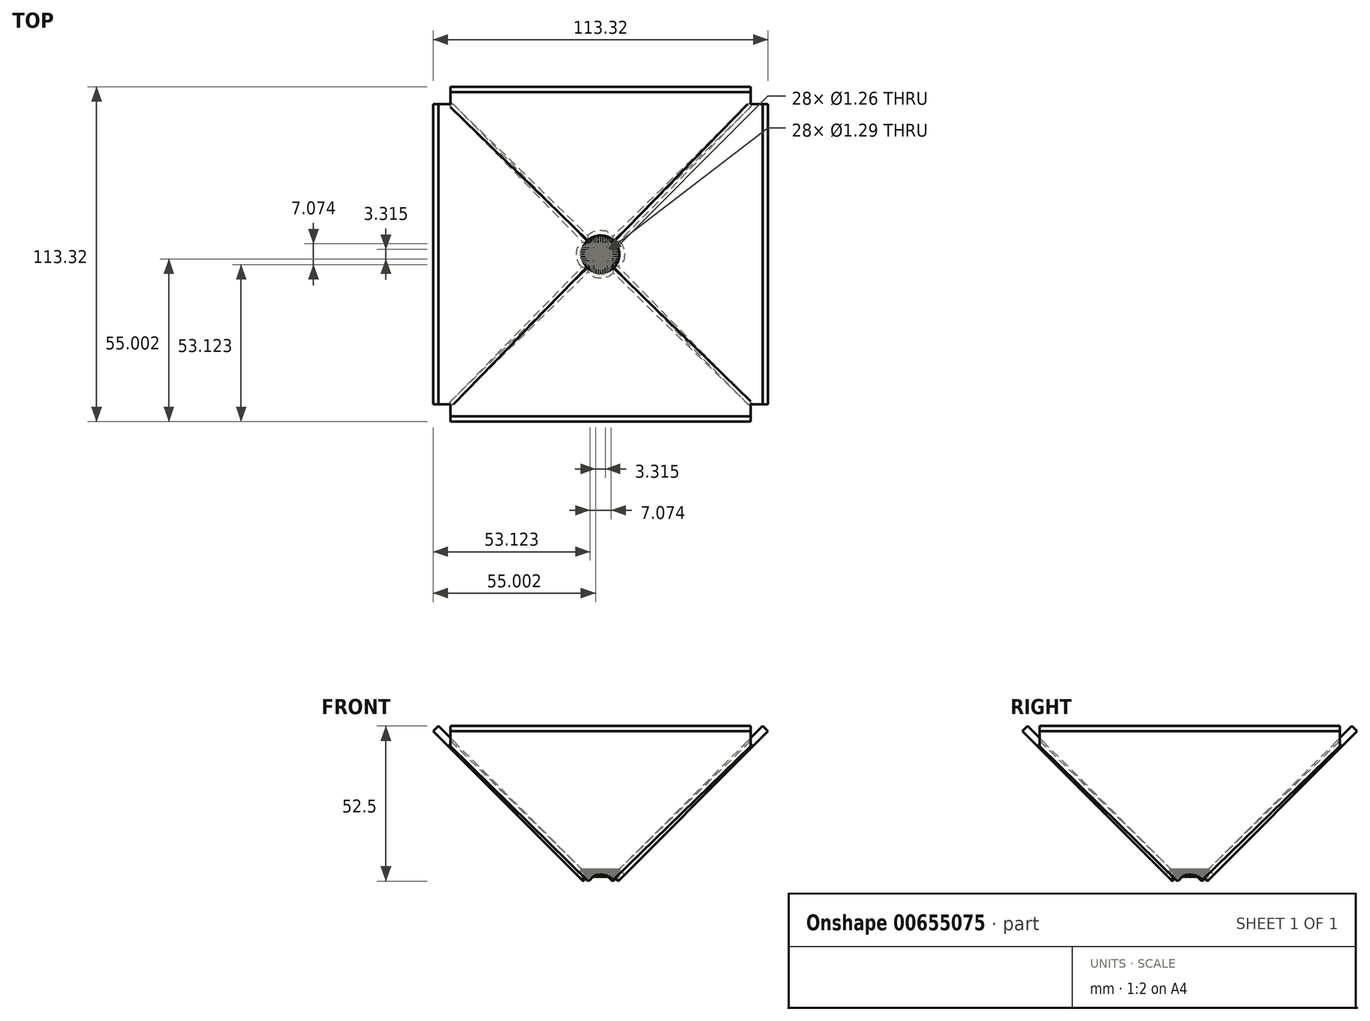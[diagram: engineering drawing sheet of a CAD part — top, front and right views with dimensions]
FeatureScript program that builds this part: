
annotation { "Feature Type Name" : "Feature", "Feature Type Description" : "" }
export const myFeature = defineFeature(function(context is Context, id is Id, definition is map)
    precondition{}
    {
        {
            var Q0;
            Q0=qCreatedBy(makeId("Top.planeOp"),FACE);
            cPlane(context, id + "F0", {"entities" : qUnion([Q0]), "cplaneType" : CPlaneType.OFFSET, "offset" : 38.1 * mm, "oppositeDirection" : true, "width" : 152.4 * mm, "height" : 152.4 * mm});
        }
        {
            var Q0;
            Q0=qCreatedBy(id+"F0.planeOp",FACE);
            var sketch = newSketch(context, id + "F1", { "sketchPlane" : qUnion([Q0])});
            skCircle(sketch, "E0", {"center": v(0, 0) * mm, "radius": 6.35 * mm});
            skCircle(sketch, "E1", {"center": v(-3.67, 3.36) * mm, "radius": 0.6 * mm});
            skCircle(sketch, "E2", {"center": v(-2.54, 2.49) * mm, "radius": 0.63 * mm});
            skCircle(sketch, "E3", {"center": v(-1.1, 1.24) * mm, "radius": 0.65 * mm});
            skCircle(sketch, "E4.1.0", {"center": v(-1.66, -0.08) * mm, "radius": 0.65 * mm});
            skCircle(sketch, "E4.1.1", {"center": v(-3.53, -0.43) * mm, "radius": 0.63 * mm});
            skCircle(sketch, "E4.1.2", {"center": v(-4.92, -0.77) * mm, "radius": 0.6 * mm});
            skCircle(sketch, "E4.2.0", {"center": v(-0.97, -1.35) * mm, "radius": 0.65 * mm});
            skCircle(sketch, "E4.2.1", {"center": v(-1.86, -3.03) * mm, "radius": 0.63 * mm});
            skCircle(sketch, "E4.2.2", {"center": v(-2.46, -4.33) * mm, "radius": 0.6 * mm});
            skCircle(sketch, "E4.3.0", {"center": v(0.45, -1.6) * mm, "radius": 0.65 * mm});
            skCircle(sketch, "E4.3.1", {"center": v(1.2, -3.34) * mm, "radius": 0.63 * mm});
            skCircle(sketch, "E4.3.2", {"center": v(1.85, -4.62) * mm, "radius": 0.6 * mm});
            skCircle(sketch, "E4.4.0", {"center": v(1.53, -0.65) * mm, "radius": 0.65 * mm});
            skCircle(sketch, "E4.4.1", {"center": v(3.37, -1.14) * mm, "radius": 0.63 * mm});
            skCircle(sketch, "E4.4.2", {"center": v(4.77, -1.44) * mm, "radius": 0.6 * mm});
            skCircle(sketch, "E4.5.0", {"center": v(1.46, 0.8) * mm, "radius": 0.65 * mm});
            skCircle(sketch, "E4.5.1", {"center": v(3, 1.92) * mm, "radius": 0.63 * mm});
            skCircle(sketch, "E4.5.2", {"center": v(4.1, 2.83) * mm, "radius": 0.6 * mm});
            skCircle(sketch, "E4.6.0", {"center": v(0.29, 1.63) * mm, "radius": 0.65 * mm});
            skCircle(sketch, "E4.6.1", {"center": v(0.36, 3.54) * mm, "radius": 0.63 * mm});
            skCircle(sketch, "E4.6.2", {"center": v(0.34, 4.97) * mm, "radius": 0.6 * mm});
            skSolve(sketch);
        }
        {
            var Q0;
            Q0=makeQuery(id+"F1.imprint","IMPRINT",FACE,{"disambiguationData":[TD([[makeQuery(id+"F1.imprint","IMPRINT",EDGE,{"derivedFrom":sQuery(id+"F1.wireOp",EDGE,"E0")}),1.0]])]});
            extrude(context, id + "F2", {"entities" : qUnion([Q0]), "oppositeDirection" : true, "depth" : 2.54 * mm, "offsetDistance" : 25.4 * mm});
        }
        {
            var Q0;
            Q0=qCreatedBy(id+"F0.planeOp",FACE);
            var sketch = newSketch(context, id + "F3", { "sketchPlane" : qUnion([Q0])});
            skLineSegment(sketch, "E5", {"start": v(6.33, -19.76) * mm, "end": v(6.33, 23.67) * mm});
            skSolve(sketch);
        }
        {
            var Q0;
            Q0=sQuery(id+"F3.wireOp",EDGE,"E5");
            cPlane(context, id + "F4", {"entities" : qUnion([Q0]), "cplaneType" : CPlaneType.LINE_ANGLE, "offset" : 25.4 * mm, "angle" : 135 * degree, "width" : 152.4 * mm, "height" : 152.4 * mm});
        }
        {
            var Q0;
            Q0=qCreatedBy(id+"F4.planeOp",FACE);
            var sketch = newSketch(context, id + "F5", { "sketchPlane" : qUnion([Q0])});
            skPoint(sketch, "E6.middle", {"position": v(0, 78.38) * mm});
            skLineSegment(sketch, "E7", {"start": v(50.8, 46.18) * mm, "end": v(50.8, 27.28) * mm});
            skLineSegment(sketch, "E8", {"start": v(-50.8, 46.18) * mm, "end": v(-50.8, 27.28) * mm});
            skPoint(sketch, "E9.start.orphan", {"position": v(0, -23.24) * mm});
            skLineSegment(sketch, "E10", {"start": v(-2.65, -23.26) * mm, "end": v(-2.65, -23.26) * mm});
            skLineSegment(sketch, "E11", {"start": v(50.8, 27.28) * mm, "end": v(5.34, -26.59) * mm});
            skFitSpline(sketch, "E12", {"points": [v(5.34, -26.59) * mm, v(4.35, -24.93) * mm, v(2.54, -23.2) * mm, v(0.28, -22.42) * mm, v(-0.8, -22.57) * mm, v(-2.12, -22.95) * mm, v(-4.13, -25.53) * mm, v(-5.03, -25.92) * mm], "startDerivative": vector(-6.1, 11.5) * mm, "endDerivative": vector(-5.47, -9.85) * mm});
            skLineSegment(sketch, "E13", {"start": v(-5.03, -25.92) * mm, "end": v(-50.8, 27.28) * mm});
            skPoint(sketch, "E6.bottom.start.orphan", {"position": v(50.8, 91.67) * mm});
            skPoint(sketch, "E6.right.start.orphan", {"position": v(-50.8, 91.67) * mm});
            skLineSegment(sketch, "E14", {"start": v(50.8, 46.18) * mm, "end": v(-50.8, 46.18) * mm});
            skPoint(sketch, "E15.orphan", {"position": v(50.8, 65.08) * mm});
            skPoint(sketch, "E16.orphan", {"position": v(-50.8, 65.08) * mm});
            skLineSegment(sketch, "E17", {"start": v(50.8, 39.03) * mm, "end": v(4.35, -24.93) * mm});
            skLineSegment(sketch, "E18", {"start": v(-50.8, 39.04) * mm, "end": v(-4.13, -25.53) * mm});
            skSolve(sketch);
        }
        {
            var Q0;
            {var subQ0=sQuery(id+"F5.wireOp",EDGE,"E14");Q0=makeQuery(id+"F5.imprint","IMPRINT",FACE,{"disambiguationData":[TD([[makeQuery(id+"F5.imprint","IMPRINT",EDGE,{"derivedFrom":subQ0}),1.0]])]});}
            extrude(context, id + "F6", {"entities" : qUnion([Q0]), "operationType" : NewBodyOperationType.ADD, "depth" : 2.54 * mm, "offsetDistance" : 25.4 * mm});
        }
        {
            var Q0;
            Q0=qCreatedBy(makeId("Front.planeOp"),FACE);
            var sketch = newSketch(context, id + "F7", { "sketchPlane" : qUnion([Q0])});
            skLineSegment(sketch, "E19", {"start": v(0, 0) * mm, "end": v(0, -3.64) * mm});
            skLineSegment(sketch, "E20", {"start": v(0, -34.92) * mm, "end": v(0, 0) * mm});
            skSolve(sketch);
        }
        {
            var Q0;
            Q0=makeQuery(id+"F2.opExtrude","SWEPT_BODY",BODY,{"disambiguationData":[OSD([sQuery(id+"F1.wireOp",EDGE,"E0"),sQuery(id+"F1.wireOp",EDGE,"E1"),sQuery(id+"F1.wireOp",EDGE,"E2"),sQuery(id+"F1.wireOp",EDGE,"E3"),sQuery(id+"F1.wireOp",EDGE,"E4.1.0"),sQuery(id+"F1.wireOp",EDGE,"E4.1.1"),sQuery(id+"F1.wireOp",EDGE,"E4.1.2"),sQuery(id+"F1.wireOp",EDGE,"E4.2.0"),sQuery(id+"F1.wireOp",EDGE,"E4.2.1"),sQuery(id+"F1.wireOp",EDGE,"E4.2.2"),sQuery(id+"F1.wireOp",EDGE,"E4.3.0"),sQuery(id+"F1.wireOp",EDGE,"E4.3.1"),sQuery(id+"F1.wireOp",EDGE,"E4.3.2"),sQuery(id+"F1.wireOp",EDGE,"E4.4.0"),sQuery(id+"F1.wireOp",EDGE,"E4.4.1"),sQuery(id+"F1.wireOp",EDGE,"E4.4.2"),sQuery(id+"F1.wireOp",EDGE,"E4.5.0"),sQuery(id+"F1.wireOp",EDGE,"E4.5.1"),sQuery(id+"F1.wireOp",EDGE,"E4.5.2"),sQuery(id+"F1.wireOp",EDGE,"E4.6.0"),sQuery(id+"F1.wireOp",EDGE,"E4.6.1"),sQuery(id+"F1.wireOp",EDGE,"E4.6.2")])]});
            var Q1;
            Q1=sQuery(id+"F7.wireOp",EDGE,"E20");
            circularPattern(context, id + "F8", {"entities" : qUnion([Q0]), "axis" : qUnion([Q1]), "angle" : 360 * degree, "instanceCount" : 4, "equalSpace" : true});
        }
    });
